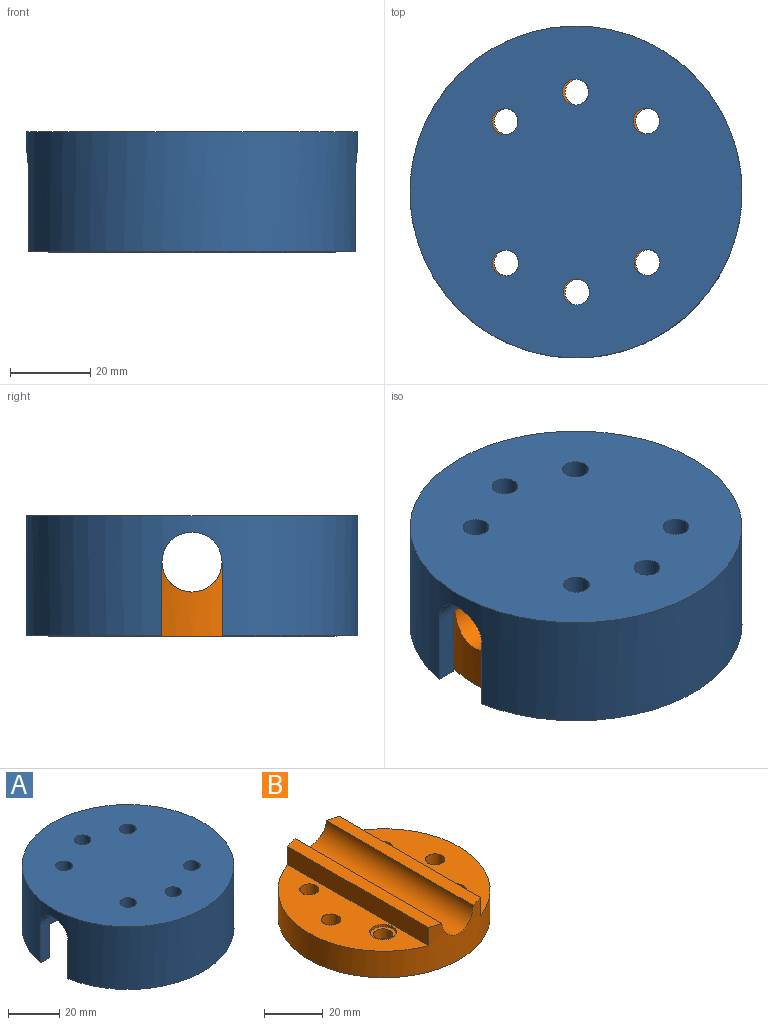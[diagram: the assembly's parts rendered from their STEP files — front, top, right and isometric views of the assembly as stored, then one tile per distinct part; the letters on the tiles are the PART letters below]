
ASSEMBLY  parts=2 mates=1
PART A: 25 faces, bbox 83x83x30 mm
  f0: cylinder r=3.25mm len=18mm, axis (0,0,-1), area 367.6mm2, adj f8,f24
  f1: plane 71.44x5mm, normal (0,0,-1), area 350.7mm2, adj f2,f18,f21
  f2: cylinder r=36.5mm len=71.44mm, axis (0,0,1), area 1173.2mm2, adj f1,f7,f14,f15,f21,f22
  f3: cylinder r=36.5mm len=71.44mm, axis (0,0,1), area 1173.2mm2, adj f4,f5,f16,f17,f19,f20
  f4: plane 71.44x5mm, normal (0,0,-1), area 350.7mm2, adj f3,f18,f19
  f5: plane 81.63x34mm, normal (0,0,-1), area 537.1mm2, adj f3,f6,f16,f17
  f6: cylinder r=41.5mm len=83mm, axis (0,0,1), area 7087.1mm2, adj f5,f7,f8,f14,f15,f16,f17,f18
  f7: plane 81.63x34mm, normal (0,0,-1), area 537.1mm2, adj f2,f6,f14,f15
  f8: plane 83x83mm, normal (0,0,1), area 5211.5mm2, adj f0,f6,f9,f10,f11,f12,f13
  f9: cylinder r=3.25mm len=19mm, axis (0,0,-1), area 388mm2, adj f8,f20
  f10: cylinder r=3.25mm len=19mm, axis (0,0,-1), area 388mm2, adj f8,f22
  f11: cylinder r=3.25mm len=19mm, axis (0,0,-1), area 388mm2, adj f8,f22
  f12: cylinder r=3.25mm len=19mm, axis (0,0,-1), area 388mm2, adj f8,f20
  f13: cylinder r=3.25mm len=19mm, axis (0,0,-1), area 388mm2, adj f8,f20
  f14: plane 18.5x5.1mm, normal (0,-1,0), area 94.3mm2, adj f2,f6,f7,f18
  f15: plane 18.5x5.1mm, normal (0,-1,0), area 94.3mm2, adj f2,f6,f7,f18
  f16: plane 18.5x5.1mm, normal (0,1,0), area 94.3mm2, adj f3,f5,f6,f18
  f17: plane 18.5x5.1mm, normal (0,1,0), area 94.3mm2, adj f3,f5,f6,f18
  f18: cylinder r=7.5mm len=83mm, axis (-1,0,0), area 1939.6mm2, adj f1,f4,f6,f14,f15,f16,f17
  f19: plane 68.59x7.5mm, normal (0,1,0), area 514.4mm2, adj f3,f4,f20
  f20: plane 68.59x24mm, normal (0,0,-1), area 1098.8mm2, adj f3,f9,f12,f13,f19
  f21: plane 68.59x7.5mm, normal (0,-1,0), area 514.4mm2, adj f1,f2,f22
  f22: plane 68.59x24mm, normal (0,0,-1), area 1068.4mm2, adj f2,f10,f11,f21,f23
  f23: cylinder r=4.5mm len=9mm, axis (0,0,-1), area 28.3mm2, adj f22,f24
  f24: plane 9x9mm, normal (0,0,-1), area 30.4mm2, adj f0,f23
PART B: 21 faces, bbox 72x72x18.5 mm
  f0: cylinder r=3.25mm len=6.5mm, axis (0,0,1), area 81.7mm2, adj f7,f20
  f1: plane 70.42x5mm, normal (0,0,1), area 345.5mm2, adj f3,f15,f18
  f2: plane 67.52x23.5mm, normal (0,0,1), area 1054.6mm2, adj f3,f12,f13,f14,f15
  f3: cylinder r=36mm len=72mm, axis (0,0,-1), area 2693.5mm2, adj f1,f2,f4,f6,f15,f16,f17,f18
  f4: plane 67.52x23.5mm, normal (0,0,1), area 1024.2mm2, adj f3,f10,f11,f16,f19
  f5: cylinder r=32mm len=64mm, axis (0,0,1), area 1206.4mm2, adj f6,f7
  f6: plane 72x72mm, normal (0,0,-1), area 854.5mm2, adj f3,f5
  f7: plane 64x64mm, normal (0,0,-1), area 2311mm2, adj f0,f5,f8,f10,f11,f12,f13,f14
  f8: cylinder r=15mm len=30mm, axis (0,0,1), area 565.5mm2, adj f7,f9
  f9: plane 30x30mm, normal (0,0,-1), area 706.9mm2, adj f8
  f10: cylinder r=3.25mm len=6.5mm, axis (0,0,1), area 102.1mm2, adj f4,f7
  f11: cylinder r=3.25mm len=6.5mm, axis (0,0,1), area 102.1mm2, adj f4,f7
  f12: cylinder r=3.25mm len=6.5mm, axis (0,0,1), area 102.1mm2, adj f2,f7
  f13: cylinder r=3.25mm len=6.5mm, axis (0,0,1), area 102.1mm2, adj f2,f7
  f14: cylinder r=3.25mm len=6.5mm, axis (0,0,1), area 102.1mm2, adj f2,f7
  f15: plane 67.52x7.5mm, normal (1,0,0), area 506.4mm2, adj f1,f2,f3
  f16: plane 67.52x7.5mm, normal (-1,0,0), area 506.4mm2, adj f3,f4,f17
  f17: plane 70.42x5mm, normal (0,0,1), area 345.5mm2, adj f3,f16,f18
  f18: cylinder r=7.5mm len=72mm, axis (0,-1,0), area 1677.9mm2, adj f1,f3,f17
  f19: cylinder r=4.5mm len=9mm, axis (0,0,1), area 28.3mm2, adj f4,f20
  f20: plane 9x9mm, normal (0,0,1), area 30.4mm2, adj f0,f19
PLACE A t=(-8.53,27.78,-3.41)mm
PLACE B rot(axis=(0,0,-1),90deg) t=(-8.53,27.78,-23.43)mm
MATE cylindrical A.f6 <-> B.f3  axis (0,0,-1) through (-8.53,27.78,-29.41)mm
